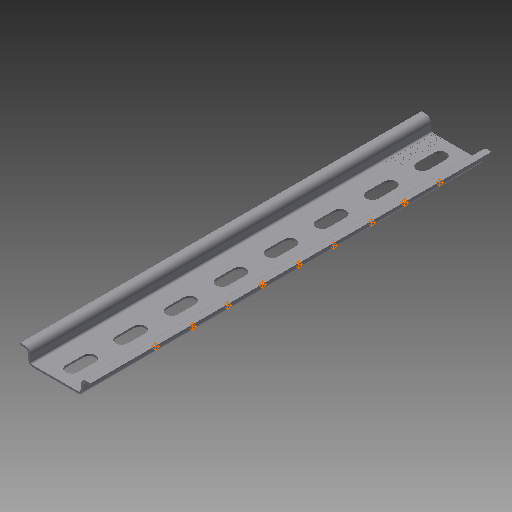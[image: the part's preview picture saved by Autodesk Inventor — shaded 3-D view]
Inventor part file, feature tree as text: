
AUTODESK INVENTOR PART (.ipt)
format: ipt  version: 2017 (Build 210142000, 142)  size: 333,312 bytes
history: native  units: in
note: dims shown in document units (in); Inventor stores cm internally (conversion verified against a paired STEP export)
features: sketch x2, other x1, plane x1, extrude x1, imported_body x1, projected_geometry x1
ambient origin geometry x8: Origin, YZ Plane, XZ Plane, XY Plane, X Axis, Y Axis, Z Axis, Center Point
bodies: Solid1 (feature_tree)
feature tree (7):
  other  "www_techna_eu-DIN 35 Rail-DEFAULT.SAT1"
  plane  "Work Plane1"
  sketch  "Sketch1"  dims[d0=7.874in d1=0.0in d2=0.0in]
  extrude  "Extrusion1"  TaperAngle=0.0deg  [1 undecoded]
  imported_body  "Base1"
  sketch  "Sketch2"
  projected_geometry  "Projected Loop1"
note: 1 required parameter value undecoded (feature->parameter linkage not recoverable at this tier; creation-order binding heuristic only, values carry confidence <= 0.55)
